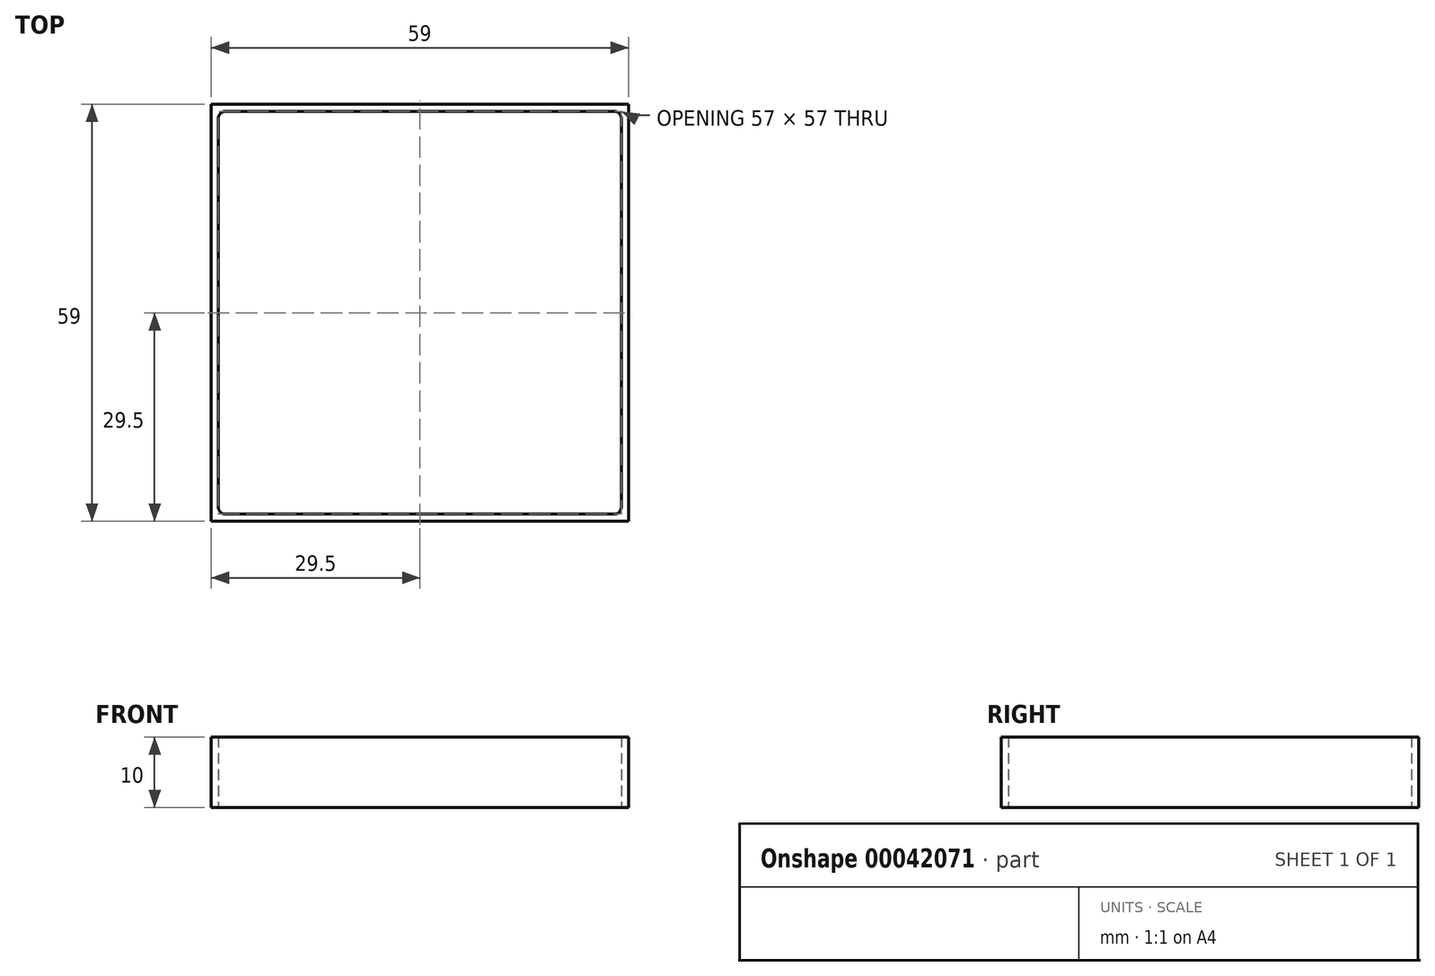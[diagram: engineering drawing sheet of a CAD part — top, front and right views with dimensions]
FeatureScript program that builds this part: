
annotation { "Feature Type Name" : "Feature", "Feature Type Description" : "" }
export const myFeature = defineFeature(function(context is Context, id is Id, definition is map)
    precondition{}
    {
        {
            var Q0;
            Q0=qCreatedBy(makeId("Top.planeOp"),FACE);
            var sketch = newSketch(context, id + "F0", { "sketchPlane" : qUnion([Q0])});
            skLineSegment(sketch, "E0.bottom", {"start": v(0, 0) * mm, "end": v(57, 0) * mm});
            skLineSegment(sketch, "E0.top", {"start": v(0, 57) * mm, "end": v(57, 57) * mm});
            skLineSegment(sketch, "E0.left", {"start": v(0, 0) * mm, "end": v(0, 57) * mm});
            skLineSegment(sketch, "E0.right", {"start": v(57, 0) * mm, "end": v(57, 57) * mm});
            skLineSegment(sketch, "E1.0", {"start": v(-1, 58) * mm, "end": v(58, 58) * mm});
            skLineSegment(sketch, "E1.1", {"start": v(-1, -1) * mm, "end": v(-1, 58) * mm});
            skLineSegment(sketch, "E1.2", {"start": v(-1, -1) * mm, "end": v(58, -1) * mm});
            skLineSegment(sketch, "E1.3", {"start": v(58, -1) * mm, "end": v(58, 58) * mm});
            skSolve(sketch);
        }
        {
            var Q0;
            Q0 = qSketchRegion(id + "F0", true);
            extrude(context, id + "F1", {"entities" : qUnion([Q0]), "depth" : 10 * mm});
        }
        {
            var Q0;
            Q0=makeQuery(id+"F1.opExtrude","SWEPT_EDGE",EDGE,{"disambiguationData":[OSD([sQuery(id+"F0.wireOp",EDGE,"E0.top"),sQuery(id+"F0.wireOp",EDGE,"E0.left")])]});
            var Q1;
            Q1=makeQuery(id+"F1.opExtrude","SWEPT_EDGE",EDGE,{"disambiguationData":[OSD([sQuery(id+"F0.wireOp",EDGE,"E0.top"),sQuery(id+"F0.wireOp",EDGE,"E0.right")])]});
            var Q2;
            Q2=makeQuery(id+"F1.opExtrude","SWEPT_EDGE",EDGE,{"disambiguationData":[OSD([sQuery(id+"F0.wireOp",EDGE,"E0.bottom"),sQuery(id+"F0.wireOp",EDGE,"E0.right")])]});
            var Q3;
            Q3=makeQuery(id+"F1.opExtrude","SWEPT_EDGE",EDGE,{"disambiguationData":[OSD([sQuery(id+"F0.wireOp",EDGE,"E0.bottom"),sQuery(id+"F0.wireOp",EDGE,"E0.left")])]});
            fillet(context, id + "F2", {"entities" : qUnion([Q0, Q1, Q2, Q3]), "radius" : 1 * mm, "tangentPropagation" : true, "allowEdgeOverflow" : false});
        }
    });
